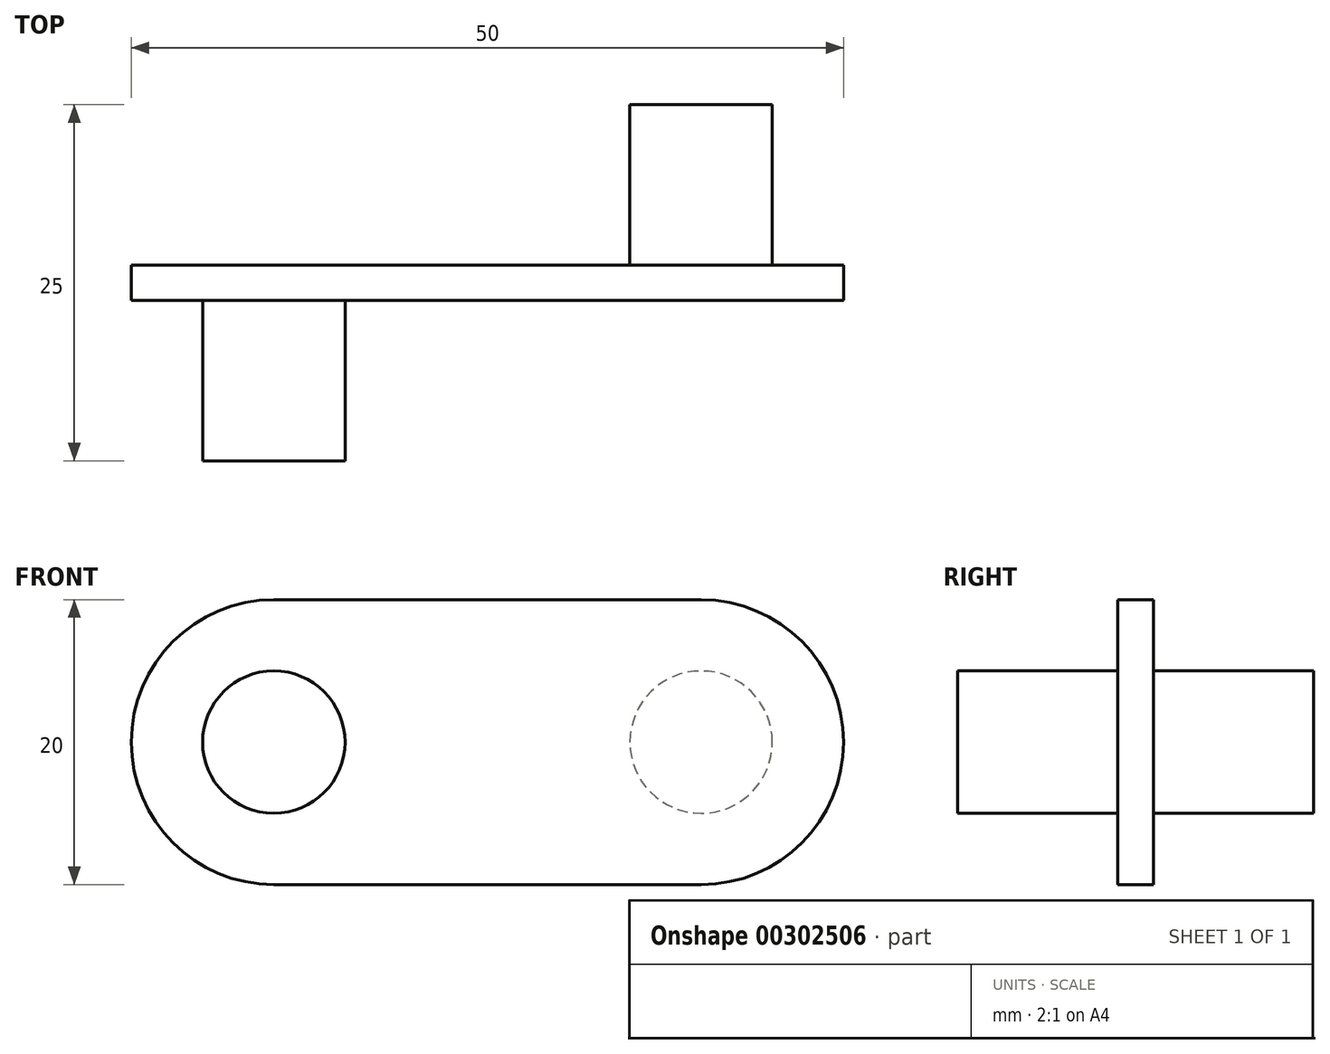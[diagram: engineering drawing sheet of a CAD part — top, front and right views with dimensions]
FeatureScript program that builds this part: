
annotation { "Feature Type Name" : "Feature", "Feature Type Description" : "" }
export const myFeature = defineFeature(function(context is Context, id is Id, definition is map)
    precondition{}
    {
        {
            var Q0;
            Q0=qCreatedBy(makeId("Front.planeOp"),FACE);
            var sketch = newSketch(context, id + "F0", { "sketchPlane" : qUnion([Q0])});
            skLineSegment(sketch, "E0.bottom", {"start": v(0, 0) * mm, "end": v(30, 0) * mm});
            skLineSegment(sketch, "E0.top", {"start": v(0, 20) * mm, "end": v(30, 20) * mm});
            skArc(sketch, "E1", {"start": v(0, 20) * mm, "mid": v(-10, 10) * mm, "end": v(0, 0) * mm});
            skArc(sketch, "E2", {"start": v(30, 0) * mm, "mid": v(40, 10) * mm, "end": v(30, 20) * mm});
            skCircle(sketch, "E3", {"center": v(0, 10) * mm, "radius": 5 * mm});
            skCircle(sketch, "E4", {"center": v(30, 10) * mm, "radius": 5 * mm});
            skSolve(sketch);
        }
        {
            var Q0;
            Q0=makeQuery(id+"F0.imprint","IMPRINT",FACE,{"disambiguationData":[TD([[makeQuery(id+"F0.imprint","IMPRINT",EDGE,{"derivedFrom":sQuery(id+"F0.wireOp",EDGE,"E0.bottom")}),1.0]])]});
            var Q1;
            Q1=makeQuery(id+"F0.imprint","IMPRINT",FACE,{"disambiguationData":[TD([[makeQuery(id+"F0.imprint","IMPRINT",EDGE,{"derivedFrom":sQuery(id+"F0.wireOp",EDGE,"E4")}),1.0]])]});
            var Q2;
            Q2=makeQuery(id+"F0.imprint","IMPRINT",FACE,{"disambiguationData":[TD([[makeQuery(id+"F0.imprint","IMPRINT",EDGE,{"derivedFrom":sQuery(id+"F0.wireOp",EDGE,"E3")}),1.0]])]});
            extrude(context, id + "F1", {"entities" : qUnion([Q0, Q1, Q2]), "endBound" : BoundingType.SYMMETRIC, "depth" : 2.5 * mm});
        }
        {
            var Q0;
            Q0=makeQuery(id+"F0.imprint","IMPRINT",FACE,{"disambiguationData":[TD([[makeQuery(id+"F0.imprint","IMPRINT",EDGE,{"derivedFrom":sQuery(id+"F0.wireOp",EDGE,"E3")}),1.0]])]});
            extrude(context, id + "F2", {"entities" : qUnion([Q0]), "operationType" : NewBodyOperationType.ADD, "depth" : 12.5 * mm});
        }
        {
            var Q0;
            Q0=makeQuery(id+"F0.imprint","IMPRINT",FACE,{"disambiguationData":[TD([[makeQuery(id+"F0.imprint","IMPRINT",EDGE,{"derivedFrom":sQuery(id+"F0.wireOp",EDGE,"E4")}),1.0]])]});
            extrude(context, id + "F3", {"entities" : qUnion([Q0]), "operationType" : NewBodyOperationType.ADD, "oppositeDirection" : true, "depth" : 12.5 * mm});
        }
    });
